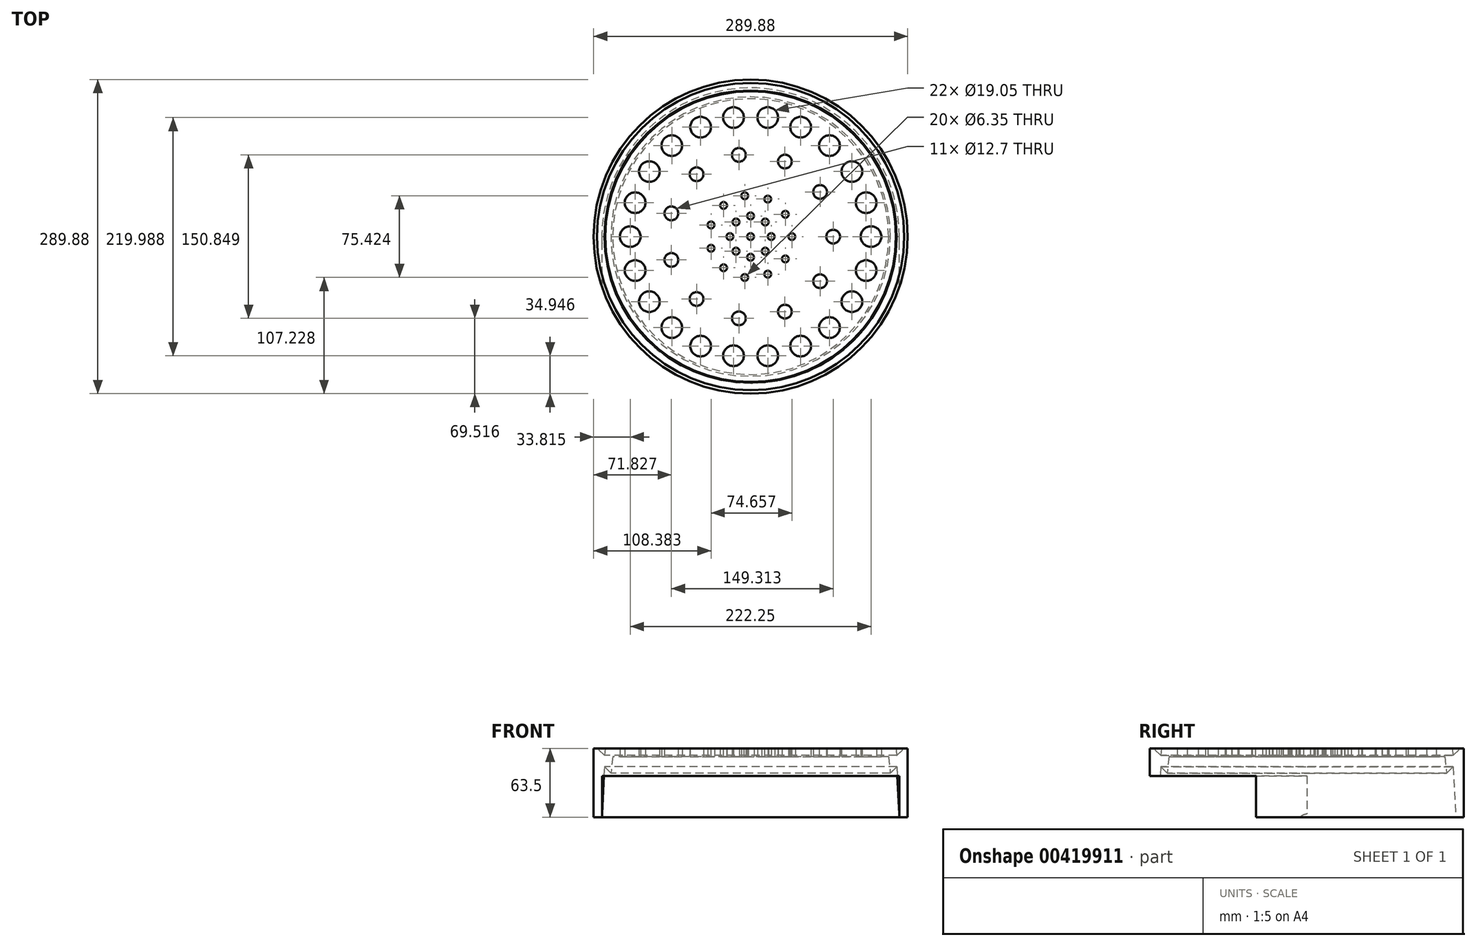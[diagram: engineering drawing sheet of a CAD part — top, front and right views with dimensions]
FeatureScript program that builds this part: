
annotation { "Feature Type Name" : "Feature", "Feature Type Description" : "" }
export const myFeature = defineFeature(function(context is Context, id is Id, definition is map)
    precondition{}
    {
        {
            var Q0;
            Q0=qCreatedBy(makeId("Front.planeOp"),FACE);
            var sketch = newSketch(context, id + "F0", { "sketchPlane" : qUnion([Q0])});
            skLineSegment(sketch, "E0", {"start": v(-144.94, 0) * mm, "end": v(-141.76, 63.5) * mm, "construction": true});
            skLineSegment(sketch, "E1", {"start": v(-141.76, 63.5) * mm, "end": v(-134.86, 56.87) * mm});
            skLineSegment(sketch, "E2", {"start": v(-134.86, 56.87) * mm, "end": v(-134.14, 63.5) * mm});
            skLineSegment(sketch, "E3", {"start": v(-134.14, 63.5) * mm, "end": v(0, 63.5) * mm, "construction": true});
            skLineSegment(sketch, "E4.0", {"start": v(-127.3, 55.88) * mm, "end": v(0, 55.88) * mm});
            skLineSegment(sketch, "E4.1", {"start": v(-128.96, 40.64) * mm, "end": v(-127.3, 55.88) * mm});
            skLineSegment(sketch, "E4.2", {"start": v(-134.99, 46.43) * mm, "end": v(-128.96, 40.64) * mm});
            skLineSegment(sketch, "E4.3", {"start": v(-137.3, 0) * mm, "end": v(-134.99, 46.43) * mm});
            skLineSegment(sketch, "E5", {"start": v(-144.94, 0) * mm, "end": v(-137.3, 0) * mm});
            skLineSegment(sketch, "E6", {"start": v(-141.76, 63.5) * mm, "end": v(-134.14, 63.5) * mm, "construction": true});
            skLineSegment(sketch, "E7", {"start": v(-137.95, 63.5) * mm, "end": v(-134.86, 56.87) * mm, "construction": true});
            skLineSegment(sketch, "E8", {"start": v(0, 63.5) * mm, "end": v(0, 0) * mm, "construction": true});
            skLineSegment(sketch, "E9", {"start": v(0, 63.5) * mm, "end": v(0, 55.88) * mm});
            skLineSegment(sketch, "E10", {"start": v(-134.14, 63.5) * mm, "end": v(0, 63.5) * mm});
            skLineSegment(sketch, "E11", {"start": v(-144.94, 63.5) * mm, "end": v(-144.94, 0) * mm});
            skLineSegment(sketch, "E12", {"start": v(-144.94, 63.5) * mm, "end": v(-141.76, 63.5) * mm});
            skSolve(sketch);
        }
        {
            var Q0;
            Q0 = qSketchRegion(id + "F0", true);
            var Q1;
            Q1=sQuery(id+"F0.wireOp",EDGE,"E8");
            revolve(context, id + "F1", {"entities" : qUnion([Q0]), "axis" : qUnion([Q1]), "revolveType" : RevolveType.FULL});
        }
        {
            var Q0;
            Q0=qCreatedBy(makeId("Front.planeOp"),FACE);
            var sketch = newSketch(context, id + "F2", { "sketchPlane" : qUnion([Q0])});
            skLineSegment(sketch, "E13.0", {"start": v(-137.3, 0) * mm, "end": v(-134.99, 46.43) * mm});
            skLineSegment(sketch, "E14.0", {"start": v(-137.3, 0) * mm, "end": v(-134.99, 46.43) * mm, "construction": true});
            skLineSegment(sketch, "E15", {"start": v(0, 0) * mm, "end": v(-137.16, 0) * mm});
            skLineSegment(sketch, "E16.0", {"start": v(-128.96, 40.64) * mm, "end": v(-127.3, 55.88) * mm});
            skLineSegment(sketch, "E17", {"start": v(-128.96, 40.64) * mm, "end": v(-133.38, 0) * mm, "construction": true});
            skLineSegment(sketch, "E18", {"start": v(-128.96, 40.64) * mm, "end": v(-128.96, 0) * mm, "construction": true});
            skLineSegment(sketch, "E19", {"start": v(-137.16, 0) * mm, "end": v(-137.16, 38.1) * mm});
            skLineSegment(sketch, "E20", {"start": v(-137.16, 38.1) * mm, "end": v(0, 38.1) * mm});
            skLineSegment(sketch, "E21.MirrorCS", {"start": v(137.16, 38.1) * mm, "end": v(0, 38.1) * mm});
            skLineSegment(sketch, "E22.MirrorCS", {"start": v(137.16, 0) * mm, "end": v(137.16, 38.1) * mm});
            skLineSegment(sketch, "E23.MirrorCS", {"start": v(0, 0) * mm, "end": v(137.16, 0) * mm});
            skSolve(sketch);
        }
        {
            var Q0;
            Q0 = qSketchRegion(id + "F2", true);
            extrude(context, id + "F3", {"entities" : qUnion([Q0]), "operationType" : NewBodyOperationType.REMOVE, "endBound" : BoundingType.THROUGH_ALL, "depth" : 25.4 * mm});
        }
        {
            var Q0;
            Q0=qCreatedBy(makeId("Top.planeOp"),FACE);
            var sketch = newSketch(context, id + "F4", { "sketchPlane" : qUnion([Q0])});
            skCircle(sketch, "E24", {"center": v(0, 0) * mm, "radius": 19.05 * mm, "construction": true});
            skCircle(sketch, "E25", {"center": v(0, 0) * mm, "radius": 38.1 * mm, "construction": true});
            skCircle(sketch, "E26", {"center": v(0, 0) * mm, "radius": 76.2 * mm, "construction": true});
            skCircle(sketch, "E27", {"center": v(19.05, 0) * mm, "radius": 3.18 * mm});
            skCircle(sketch, "E28.1.0", {"center": v(13.47, 13.47) * mm, "radius": 3.18 * mm});
            skCircle(sketch, "E28.2.0", {"center": v(0, 19.05) * mm, "radius": 3.18 * mm});
            skCircle(sketch, "E29.1.3.0", {"center": v(-13.47, 13.47) * mm, "radius": 3.18 * mm});
            skCircle(sketch, "E29.1.4.0", {"center": v(-19.05, 0) * mm, "radius": 3.18 * mm});
            skCircle(sketch, "E29.1.5.0", {"center": v(-13.47, -13.47) * mm, "radius": 3.18 * mm});
            skCircle(sketch, "E29.1.6.0", {"center": v(0, -19.05) * mm, "radius": 3.18 * mm});
            skCircle(sketch, "E29.1.7.0", {"center": v(13.47, -13.47) * mm, "radius": 3.18 * mm});
            skCircle(sketch, "E30", {"center": v(38.1, 0) * mm, "radius": 3.18 * mm});
            skCircle(sketch, "E31.1.0", {"center": v(32.05, 20.6) * mm, "radius": 3.17 * mm});
            skCircle(sketch, "E31.2.0", {"center": v(15.83, 34.66) * mm, "radius": 3.17 * mm});
            skCircle(sketch, "E32", {"center": v(76.2, 0) * mm, "radius": 6.35 * mm});
            skCircle(sketch, "E33.1.3.0", {"center": v(-5.42, 37.71) * mm, "radius": 3.18 * mm});
            skCircle(sketch, "E33.1.4.0", {"center": v(-24.95, 28.8) * mm, "radius": 3.18 * mm});
            skCircle(sketch, "E33.1.5.0", {"center": v(-36.56, 10.73) * mm, "radius": 3.18 * mm});
            skCircle(sketch, "E33.1.6.0", {"center": v(-36.56, -10.73) * mm, "radius": 3.18 * mm});
            skCircle(sketch, "E33.1.7.0", {"center": v(-24.95, -28.8) * mm, "radius": 3.18 * mm});
            skCircle(sketch, "E33.1.8.0", {"center": v(-5.42, -37.71) * mm, "radius": 3.18 * mm});
            skCircle(sketch, "E33.1.9.0", {"center": v(15.83, -34.66) * mm, "radius": 3.18 * mm});
            skCircle(sketch, "E33.1.10.0", {"center": v(32.05, -20.6) * mm, "radius": 3.18 * mm});
            skCircle(sketch, "E34.1.0", {"center": v(64.1, 41.2) * mm, "radius": 6.35 * mm});
            skCircle(sketch, "E34.2.0", {"center": v(31.65, 69.31) * mm, "radius": 6.35 * mm});
            skCircle(sketch, "E35.1.3.0", {"center": v(-10.84, 75.42) * mm, "radius": 6.35 * mm});
            skCircle(sketch, "E35.1.4.0", {"center": v(-49.9, 57.59) * mm, "radius": 6.35 * mm});
            skCircle(sketch, "E35.1.5.0", {"center": v(-73.11, 21.47) * mm, "radius": 6.35 * mm});
            skCircle(sketch, "E35.1.6.0", {"center": v(-73.11, -21.47) * mm, "radius": 6.35 * mm});
            skCircle(sketch, "E35.1.7.0", {"center": v(-49.9, -57.59) * mm, "radius": 6.35 * mm});
            skCircle(sketch, "E36.1.8.0", {"center": v(-10.84, -75.42) * mm, "radius": 6.35 * mm});
            skCircle(sketch, "E37.1.9.0", {"center": v(31.65, -69.31) * mm, "radius": 6.35 * mm});
            skCircle(sketch, "E38.1.10.0", {"center": v(64.1, -41.2) * mm, "radius": 6.35 * mm});
            skCircle(sketch, "E39", {"center": v(0, 0) * mm, "radius": 3.18 * mm});
            skCircle(sketch, "E40", {"center": v(0, 0) * mm, "radius": 111.13 * mm, "construction": true});
            skCircle(sketch, "E41", {"center": v(111.13, 0) * mm, "radius": 9.53 * mm});
            skCircle(sketch, "E42.1.0", {"center": v(106.62, 31.3) * mm, "radius": 9.52 * mm});
            skCircle(sketch, "E42.2.0", {"center": v(93.48, 60.08) * mm, "radius": 9.52 * mm});
            skCircle(sketch, "E43.1.3.0", {"center": v(72.77, 83.98) * mm, "radius": 9.52 * mm});
            skCircle(sketch, "E43.1.4.0", {"center": v(46.16, 101.08) * mm, "radius": 9.52 * mm});
            skCircle(sketch, "E43.1.5.0", {"center": v(15.81, 110) * mm, "radius": 9.52 * mm});
            skCircle(sketch, "E43.1.6.0", {"center": v(-15.81, 110) * mm, "radius": 9.52 * mm});
            skCircle(sketch, "E43.1.7.0", {"center": v(-46.16, 101.08) * mm, "radius": 9.52 * mm});
            skCircle(sketch, "E43.1.8.0", {"center": v(-72.77, 83.98) * mm, "radius": 9.52 * mm});
            skCircle(sketch, "E43.1.9.0", {"center": v(-93.48, 60.08) * mm, "radius": 9.52 * mm});
            skCircle(sketch, "E43.1.10.0", {"center": v(-106.62, 31.3) * mm, "radius": 9.52 * mm});
            skCircle(sketch, "E44.1.11.0", {"center": v(-111.12, 0) * mm, "radius": 9.53 * mm});
            skCircle(sketch, "E45.1.12.0", {"center": v(-106.62, -31.3) * mm, "radius": 9.52 * mm});
            skCircle(sketch, "E46.1.13.0", {"center": v(-93.48, -60.08) * mm, "radius": 9.52 * mm});
            skCircle(sketch, "E47.1.14.0", {"center": v(-72.77, -83.98) * mm, "radius": 9.52 * mm});
            skCircle(sketch, "E48.1.15.0", {"center": v(-46.16, -101.08) * mm, "radius": 9.52 * mm});
            skCircle(sketch, "E49.1.16.0", {"center": v(-15.81, -110) * mm, "radius": 9.52 * mm});
            skCircle(sketch, "E50.1.17.0", {"center": v(15.81, -110) * mm, "radius": 9.53 * mm});
            skCircle(sketch, "E51.1.18.0", {"center": v(46.16, -101.08) * mm, "radius": 9.53 * mm});
            skCircle(sketch, "E52.1.19.0", {"center": v(72.77, -83.98) * mm, "radius": 9.53 * mm});
            skCircle(sketch, "E53.1.20.0", {"center": v(93.48, -60.08) * mm, "radius": 9.53 * mm});
            skCircle(sketch, "E54.1.21.0", {"center": v(106.62, -31.3) * mm, "radius": 9.52 * mm});
            skSolve(sketch);
        }
        {
            var Q0;
            Q0 = qSketchRegion(id + "F4", true);
            extrude(context, id + "F5", {"entities" : qUnion([Q0]), "operationType" : NewBodyOperationType.REMOVE, "endBound" : BoundingType.THROUGH_ALL, "depth" : 25.4 * mm});
        }
    });
